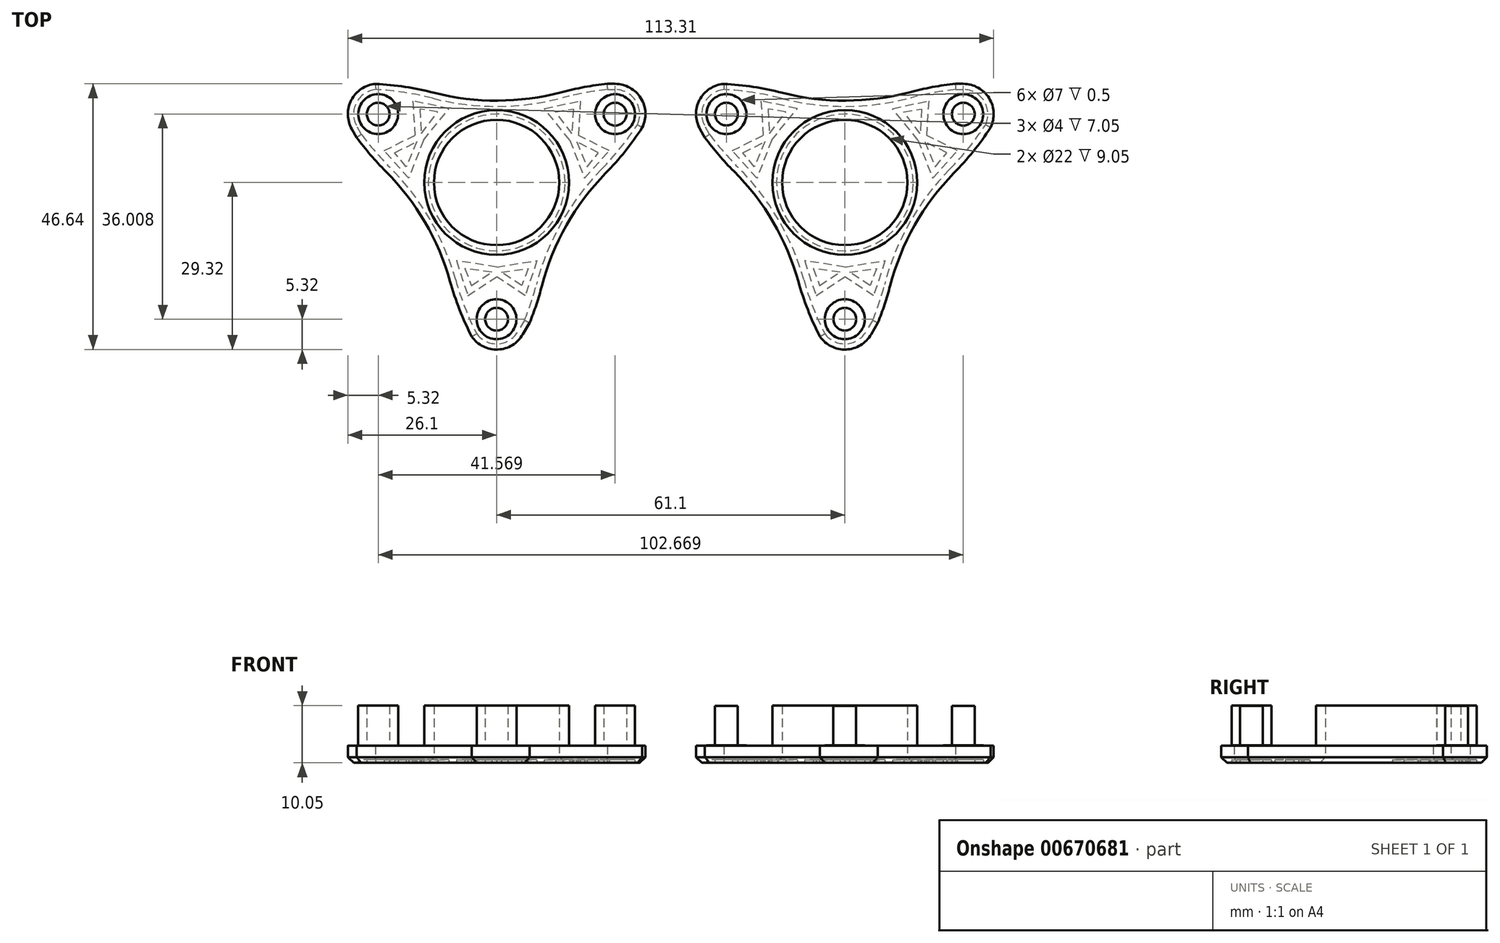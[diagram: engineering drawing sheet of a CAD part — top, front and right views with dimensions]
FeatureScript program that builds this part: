
annotation { "Feature Type Name" : "Feature", "Feature Type Description" : "" }
export const myFeature = defineFeature(function(context is Context, id is Id, definition is map)
    precondition{}
    {
        {
            var Q0;
            Q0=qCreatedBy(makeId("Top.planeOp"),FACE);
            var sketch = newSketch(context, id + "F0", { "sketchPlane" : qUnion([Q0])});
            skLineSegment(sketch, "E0.0", {"start": v(-30, 17.3) * mm, "end": v(30, 17.33) * mm});
            skLineSegment(sketch, "E0.1", {"start": v(30, 17.33) * mm, "end": v(0.02, -34.64) * mm});
            skLineSegment(sketch, "E0.2", {"start": v(0.02, -34.64) * mm, "end": v(-30, 17.3) * mm});
            skPoint(sketch, "E0.0.midPoint", {"position": v(0, 17.32) * mm});
            skLineSegment(sketch, "E1.0", {"start": v(0, 59) * mm, "end": v(50.95, -29.25) * mm, "construction": true});
            skLineSegment(sketch, "E1.1", {"start": v(50.95, -29.25) * mm, "end": v(-50.66, -29.25) * mm, "construction": true});
            skLineSegment(sketch, "E1.2", {"start": v(-50.66, -29.25) * mm, "end": v(0, 59) * mm, "construction": true});
            skCircle(sketch, "E2", {"center": v(-50.66, -29.25) * mm, "radius": 44.13 * mm});
            skCircle(sketch, "E3.1.0", {"center": v(50.66, -29.25) * mm, "radius": 44.13 * mm});
            skCircle(sketch, "E3.2.0", {"center": v(0, 58.5) * mm, "radius": 44.13 * mm});
            skPoint(sketch, "E3.center", {"position": v(0, 0) * mm});
            skPoint(sketch, "E4.0.midPoint", {"position": v(0, 14.36) * mm});
            skCircle(sketch, "E5", {"center": v(-20.78, 12) * mm, "radius": 3.5 * mm});
            skCircle(sketch, "E6.1.0", {"center": v(0, -24) * mm, "radius": 3.5 * mm});
            skCircle(sketch, "E6.2.0", {"center": v(20.79, 12) * mm, "radius": 3.5 * mm});
            skCircle(sketch, "E7", {"center": v(0, 0) * mm, "radius": 11 * mm});
            skCircle(sketch, "E8", {"center": v(0, 0) * mm, "radius": 12.7 * mm});
            skCircle(sketch, "E9", {"center": v(-20.78, 12) * mm, "radius": 2 * mm});
            skCircle(sketch, "E10.1.0", {"center": v(0, -24) * mm, "radius": 2 * mm});
            skCircle(sketch, "E10.2.0", {"center": v(20.79, 12) * mm, "radius": 2 * mm});
            skArc(sketch, "E11", {"start": v(25.22, 9.04) * mm, "mid": v(25.48, 14.5) * mm, "end": v(20.79, 17.32) * mm});
            skArc(sketch, "E12.1.0", {"start": v(-20.44, 17.32) * mm, "mid": v(-25.3, 14.81) * mm, "end": v(-25.4, 9.35) * mm});
            skArc(sketch, "E12.2.0", {"start": v(-4.78, -26.36) * mm, "mid": v(-0.18, -29.32) * mm, "end": v(4.6, -26.66) * mm});
            skLineSegment(sketch, "E13", {"start": v(20.79, 17.32) * mm, "end": v(19.44, 17.32) * mm});
            skLineSegment(sketch, "E14", {"start": v(-25.4, 9.35) * mm, "end": v(-24.56, 7.9) * mm});
            skLineSegment(sketch, "E15", {"start": v(-20.44, 17.32) * mm, "end": v(-19.08, 17.31) * mm});
            skLineSegment(sketch, "E16", {"start": v(25.22, 9.04) * mm, "end": v(24.03, 6.97) * mm});
            skLineSegment(sketch, "E17", {"start": v(4.6, -26.66) * mm, "end": v(5.8, -24.63) * mm});
            skLineSegment(sketch, "E18", {"start": v(-4.78, -26.36) * mm, "end": v(-5.84, -24.51) * mm});
            skLineSegment(sketch, "E19", {"start": v(-7.07, -13.73) * mm, "end": v(-5.04, -19.9) * mm});
            skLineSegment(sketch, "E20", {"start": v(-5.04, -19.9) * mm, "end": v(0, -16.56) * mm});
            skLineSegment(sketch, "E21", {"start": v(0, -14.83) * mm, "end": v(-7.07, -13.73) * mm});
            skLineSegment(sketch, "E22", {"start": v(-5.56, -15.13) * mm, "end": v(-4.42, -18.1) * mm});
            skLineSegment(sketch, "E23", {"start": v(-4.42, -18.1) * mm, "end": v(-0.83, -15.74) * mm});
            skLineSegment(sketch, "E24", {"start": v(-0.83, -15.74) * mm, "end": v(-5.56, -15.13) * mm});
            skLineSegment(sketch, "E25.MirrorCS", {"start": v(5.04, -19.9) * mm, "end": v(0, -16.56) * mm});
            skLineSegment(sketch, "E26.MirrorCS", {"start": v(7.07, -13.73) * mm, "end": v(5.04, -19.9) * mm});
            skLineSegment(sketch, "E27.MirrorCS", {"start": v(0.83, -15.74) * mm, "end": v(5.56, -15.13) * mm});
            skLineSegment(sketch, "E28.MirrorCS", {"start": v(5.56, -15.13) * mm, "end": v(4.42, -18.1) * mm});
            skLineSegment(sketch, "E29.MirrorCS", {"start": v(4.42, -18.1) * mm, "end": v(0.83, -15.74) * mm});
            skLineSegment(sketch, "E30.MirrorCS", {"start": v(0, -14.83) * mm, "end": v(7.07, -13.73) * mm});
            skLineSegment(sketch, "E31.1.0", {"start": v(15.42, 0.74) * mm, "end": v(19.75, 5.58) * mm});
            skLineSegment(sketch, "E31.1.1", {"start": v(12.85, 7.42) * mm, "end": v(15.42, 0.74) * mm});
            skLineSegment(sketch, "E31.1.2", {"start": v(14.04, 7.15) * mm, "end": v(15.89, 2.76) * mm});
            skLineSegment(sketch, "E31.1.3", {"start": v(17.88, 5.22) * mm, "end": v(14.04, 7.15) * mm});
            skLineSegment(sketch, "E31.1.4", {"start": v(15.89, 2.76) * mm, "end": v(17.88, 5.22) * mm});
            skLineSegment(sketch, "E31.1.5", {"start": v(19.75, 5.58) * mm, "end": v(14.34, 8.28) * mm});
            skLineSegment(sketch, "E31.1.6", {"start": v(14.7, 14.31) * mm, "end": v(14.34, 8.28) * mm});
            skLineSegment(sketch, "E31.1.7", {"start": v(13.46, 12.88) * mm, "end": v(13.22, 8.58) * mm});
            skLineSegment(sketch, "E31.1.8", {"start": v(13.22, 8.58) * mm, "end": v(10.33, 12.38) * mm});
            skLineSegment(sketch, "E31.1.9", {"start": v(10.33, 12.38) * mm, "end": v(13.46, 12.88) * mm});
            skLineSegment(sketch, "E31.1.10", {"start": v(12.85, 7.42) * mm, "end": v(8.35, 12.98) * mm});
            skLineSegment(sketch, "E31.1.11", {"start": v(8.35, 12.98) * mm, "end": v(14.7, 14.31) * mm});
            skLineSegment(sketch, "E31.2.0", {"start": v(-8.35, 12.98) * mm, "end": v(-14.7, 14.31) * mm});
            skLineSegment(sketch, "E31.2.1", {"start": v(-12.85, 7.42) * mm, "end": v(-8.35, 12.98) * mm});
            skLineSegment(sketch, "E31.2.2", {"start": v(-13.22, 8.58) * mm, "end": v(-10.33, 12.38) * mm});
            skLineSegment(sketch, "E31.2.3", {"start": v(-13.46, 12.88) * mm, "end": v(-13.22, 8.58) * mm});
            skLineSegment(sketch, "E31.2.4", {"start": v(-10.33, 12.38) * mm, "end": v(-13.46, 12.88) * mm});
            skLineSegment(sketch, "E31.2.5", {"start": v(-14.7, 14.31) * mm, "end": v(-14.34, 8.28) * mm});
            skLineSegment(sketch, "E31.2.6", {"start": v(-19.75, 5.58) * mm, "end": v(-14.34, 8.28) * mm});
            skLineSegment(sketch, "E31.2.7", {"start": v(-17.88, 5.22) * mm, "end": v(-14.04, 7.15) * mm});
            skLineSegment(sketch, "E31.2.8", {"start": v(-14.04, 7.15) * mm, "end": v(-15.89, 2.76) * mm});
            skLineSegment(sketch, "E31.2.9", {"start": v(-15.89, 2.76) * mm, "end": v(-17.88, 5.22) * mm});
            skLineSegment(sketch, "E31.2.10", {"start": v(-12.85, 7.42) * mm, "end": v(-15.42, 0.74) * mm});
            skLineSegment(sketch, "E31.2.11", {"start": v(-15.42, 0.74) * mm, "end": v(-19.75, 5.58) * mm});
            skSolve(sketch);
        }
        {
            var Q0;
            Q0=makeQuery(id+"F0.imprint","IMPRINT",FACE,{"disambiguationData":[TD([[makeQuery(id+"F0.imprint","IMPRINT",EDGE,{"derivedFrom":sQuery(id+"F0.wireOp",EDGE,"E5")}),-1.0]])]});
            var Q1;
            Q1=makeQuery(id+"F0.imprint","IMPRINT",FACE,{"disambiguationData":[TD([[makeQuery(id+"F0.imprint","IMPRINT",EDGE,{"derivedFrom":sQuery(id+"F0.wireOp",EDGE,"E9")}),1.0]])]});
            var Q2;
            Q2=makeQuery(id+"F0.imprint","IMPRINT",FACE,{"disambiguationData":[TD([[makeQuery(id+"F0.imprint","IMPRINT",EDGE,{"derivedFrom":sQuery(id+"F0.wireOp",EDGE,"E10.2.0")}),1.0]])]});
            var Q3;
            Q3=makeQuery(id+"F0.imprint","IMPRINT",FACE,{"disambiguationData":[TD([[makeQuery(id+"F0.imprint","IMPRINT",EDGE,{"derivedFrom":sQuery(id+"F0.wireOp",EDGE,"E10.1.0")}),1.0]])]});
            var Q4;
            Q4=makeQuery(id+"F0.imprint","IMPRINT",FACE,{"disambiguationData":[TD([[makeQuery(id+"F0.imprint","IMPRINT",EDGE,{"derivedFrom":sQuery(id+"F0.wireOp",EDGE,"E19")}),1.0]])]});
            var Q5;
            Q5=makeQuery(id+"F0.imprint","IMPRINT",FACE,{"disambiguationData":[TD([[makeQuery(id+"F0.imprint","IMPRINT",EDGE,{"derivedFrom":sQuery(id+"F0.wireOp",EDGE,"E27.MirrorCS")}),-1.0]])]});
            var Q6;
            Q6=makeQuery(id+"F0.imprint","IMPRINT",FACE,{"disambiguationData":[TD([[makeQuery(id+"F0.imprint","IMPRINT",EDGE,{"derivedFrom":sQuery(id+"F0.wireOp",EDGE,"E22")}),1.0]])]});
            var Q7;
            Q7=makeQuery(id+"F0.imprint","IMPRINT",FACE,{"disambiguationData":[TD([[makeQuery(id+"F0.imprint","IMPRINT",EDGE,{"derivedFrom":sQuery(id+"F0.wireOp",EDGE,"E31.1.0")}),1.0]])]});
            var Q8;
            Q8=makeQuery(id+"F0.imprint","IMPRINT",FACE,{"disambiguationData":[TD([[makeQuery(id+"F0.imprint","IMPRINT",EDGE,{"derivedFrom":sQuery(id+"F0.wireOp",EDGE,"E31.1.2")}),1.0]])]});
            var Q9;
            Q9=makeQuery(id+"F0.imprint","IMPRINT",FACE,{"disambiguationData":[TD([[makeQuery(id+"F0.imprint","IMPRINT",EDGE,{"derivedFrom":sQuery(id+"F0.wireOp",EDGE,"E31.1.7")}),-1.0]])]});
            var Q10;
            Q10=makeQuery(id+"F0.imprint","IMPRINT",FACE,{"disambiguationData":[TD([[makeQuery(id+"F0.imprint","IMPRINT",EDGE,{"derivedFrom":sQuery(id+"F0.wireOp",EDGE,"E31.2.0")}),1.0]])]});
            var Q11;
            Q11=makeQuery(id+"F0.imprint","IMPRINT",FACE,{"disambiguationData":[TD([[makeQuery(id+"F0.imprint","IMPRINT",EDGE,{"derivedFrom":sQuery(id+"F0.wireOp",EDGE,"E31.2.2")}),1.0]])]});
            var Q12;
            Q12=makeQuery(id+"F0.imprint","IMPRINT",FACE,{"disambiguationData":[TD([[makeQuery(id+"F0.imprint","IMPRINT",EDGE,{"derivedFrom":sQuery(id+"F0.wireOp",EDGE,"E31.2.7")}),-1.0]])]});
            extrude(context, id + "F1", {"entities" : qUnion([Q0, Q1, Q2, Q3, Q4, Q5, Q6, Q7, Q8, Q9, Q10, Q11, Q12]), "depth" : 3 * mm, "offsetDistance" : 25 * mm});
        }
        {
            var Q0;
            Q0=makeQuery(id+"F0.imprint","IMPRINT",FACE,{"disambiguationData":[TD([[makeQuery(id+"F0.imprint","IMPRINT",EDGE,{"derivedFrom":sQuery(id+"F0.wireOp",EDGE,"E5")}),1.0]])]});
            var Q1;
            Q1=makeQuery(id+"F0.imprint","IMPRINT",FACE,{"disambiguationData":[TD([[makeQuery(id+"F0.imprint","IMPRINT",EDGE,{"derivedFrom":sQuery(id+"F0.wireOp",EDGE,"E6.1.0")}),1.0]])]});
            var Q2;
            Q2=makeQuery(id+"F0.imprint","IMPRINT",FACE,{"disambiguationData":[TD([[makeQuery(id+"F0.imprint","IMPRINT",EDGE,{"derivedFrom":sQuery(id+"F0.wireOp",EDGE,"E6.2.0")}),1.0]])]});
            var Q3;
            Q3=makeQuery(id+"F0.imprint","IMPRINT",FACE,{"disambiguationData":[TD([[makeQuery(id+"F0.imprint","IMPRINT",EDGE,{"derivedFrom":sQuery(id+"F0.wireOp",EDGE,"E7")}),-1.0]])]});
            extrude(context, id + "F2", {"entities" : qUnion([Q0, Q1, Q2, Q3]), "operationType" : NewBodyOperationType.ADD, "depth" : 10.05 * mm, "offsetDistance" : 25 * mm});
        }
        {
            var Q0;
            {var subQ0=sQuery(id+"F0.wireOp",EDGE,"E3.1.0");var subQ1=sQuery(id+"F0.wireOp",EDGE,"E0.1");Q0=makeQuery(id+"F1.opExtrude","SWEPT_EDGE",EDGE,{"disambiguationData":[OSD([subQ1,subQ0]),TDD([makeQuery(id+"F0.imprint","INTERSECT",VERTEX,{"disambiguationData":[OD(0.0)],"derivedFrom":[subQ1,subQ0]})])]});}
            var Q1;
            {var subQ0=sQuery(id+"F0.wireOp",EDGE,"E3.2.0");var subQ1=sQuery(id+"F0.wireOp",EDGE,"E0.0");Q1=makeQuery(id+"F1.opExtrude","SWEPT_EDGE",EDGE,{"disambiguationData":[OSD([subQ1,subQ0]),TDD([makeQuery(id+"F0.imprint","INTERSECT",VERTEX,{"disambiguationData":[OD(1.0)],"derivedFrom":[subQ1,subQ0]})])]});}
            var Q2;
            {var subQ0=sQuery(id+"F0.wireOp",EDGE,"E3.2.0");var subQ1=sQuery(id+"F0.wireOp",EDGE,"E0.0");Q2=makeQuery(id+"F1.opExtrude","SWEPT_EDGE",EDGE,{"disambiguationData":[OSD([subQ1,subQ0]),TDD([makeQuery(id+"F0.imprint","INTERSECT",VERTEX,{"disambiguationData":[OD(0.0)],"derivedFrom":[subQ1,subQ0]})])]});}
            var Q3;
            {var subQ0=sQuery(id+"F0.wireOp",EDGE,"E2");var subQ1=sQuery(id+"F0.wireOp",EDGE,"E0.2");Q3=makeQuery(id+"F1.opExtrude","SWEPT_EDGE",EDGE,{"disambiguationData":[OSD([subQ1,subQ0]),TDD([makeQuery(id+"F0.imprint","INTERSECT",VERTEX,{"disambiguationData":[OD(1.0)],"derivedFrom":[subQ1,subQ0]})])]});}
            var Q4;
            {var subQ0=sQuery(id+"F0.wireOp",EDGE,"E2");var subQ1=sQuery(id+"F0.wireOp",EDGE,"E0.2");Q4=makeQuery(id+"F1.opExtrude","SWEPT_EDGE",EDGE,{"disambiguationData":[OSD([subQ1,subQ0]),TDD([makeQuery(id+"F0.imprint","INTERSECT",VERTEX,{"disambiguationData":[OD(0.0)],"derivedFrom":[subQ1,subQ0]})])]});}
            var Q5;
            {var subQ0=sQuery(id+"F0.wireOp",EDGE,"E3.1.0");var subQ1=sQuery(id+"F0.wireOp",EDGE,"E0.1");Q5=makeQuery(id+"F1.opExtrude","SWEPT_EDGE",EDGE,{"disambiguationData":[OSD([subQ1,subQ0]),TDD([makeQuery(id+"F0.imprint","INTERSECT",VERTEX,{"disambiguationData":[OD(1.0)],"derivedFrom":[subQ1,subQ0]})])]});}
            fillet(context, id + "F3", {"entities" : qUnion([Q0, Q1, Q2, Q3, Q4, Q5]), "radius" : 52.19 * mm, "tangentPropagation" : true, "allowEdgeOverflow" : false});
        }
        {
            var Q0;
            {var subQ0=sQuery(id+"F0.wireOp",EDGE,"E8");var subQ1=sQuery(id+"F0.wireOp",EDGE,"E10.2.0");var subQ2=sQuery(id+"F0.wireOp",EDGE,"E6.2.0");var subQ3=sQuery(id+"F0.wireOp",EDGE,"E10.1.0");var subQ4=sQuery(id+"F0.wireOp",EDGE,"E6.1.0");var subQ5=sQuery(id+"F0.wireOp",EDGE,"E9");var subQ6=sQuery(id+"F0.wireOp",EDGE,"E5");Q0=makeQuery(id+"F2.boolean.opBoolean","MERGE",FACE,{"derivedFrom":[makeQuery(id+"F1.opExtrude","CAP_FACE",FACE,{"disambiguationData":[OSD([sQuery(id+"F0.wireOp",EDGE,"E0.0"),sQuery(id+"F0.wireOp",EDGE,"E0.1"),sQuery(id+"F0.wireOp",EDGE,"E0.2"),sQuery(id+"F0.wireOp",EDGE,"E2"),sQuery(id+"F0.wireOp",EDGE,"E3.1.0"),sQuery(id+"F0.wireOp",EDGE,"E3.2.0"),subQ6,subQ4,subQ2,subQ0,sQuery(id+"F0.wireOp",EDGE,"1SJySKtc-A8GW-sxNI-XXrC-uOoADmk9XYJx"),sQuery(id+"F0.wireOp",EDGE,"85b40759-12c6-4cf2-8159-2576a97e2fa2.1.0"),sQuery(id+"F0.wireOp",EDGE,"85b40759-12c6-4cf2-8159-2576a97e2fa2.2.0"),sQuery(id+"F0.wireOp",EDGE,"dcBHJXyL-KOau-6C6y-PPaA-2r918rPn5gXJ"),sQuery(id+"F0.wireOp",EDGE,"AZoCeLLD-ZZL2-adv5-qf0w-prbMICUiqzPw"),sQuery(id+"F0.wireOp",EDGE,"4dO1bbNr-65Ks-fPpC-CJ1R-cWI9Ptmbnuol")])],"isStart":true}),makeQuery(id+"F1.opExtrude","CAP_FACE",FACE,{"disambiguationData":[OSD([subQ5])],"isStart":true}),makeQuery(id+"F1.opExtrude","CAP_FACE",FACE,{"disambiguationData":[OSD([subQ3])],"isStart":true}),makeQuery(id+"F1.opExtrude","CAP_FACE",FACE,{"disambiguationData":[OSD([subQ1])],"isStart":true}),makeQuery(id+"F2.opExtrude","CAP_FACE",FACE,{"disambiguationData":[OSD([subQ6,subQ5])],"isStart":true}),makeQuery(id+"F2.opExtrude","CAP_FACE",FACE,{"disambiguationData":[OSD([subQ4,subQ3])],"isStart":true}),makeQuery(id+"F2.opExtrude","CAP_FACE",FACE,{"disambiguationData":[OSD([subQ2,subQ1])],"isStart":true}),makeQuery(id+"F2.opExtrude","CAP_FACE",FACE,{"disambiguationData":[OSD([sQuery(id+"F0.wireOp",EDGE,"E7"),subQ0])],"isStart":true})]});}
            chamfer(context, id + "F4", {"entities" : qUnion([Q0]), "width" : 1 * mm, "tangentPropagation" : true});
        }
        {
            var Q0;
            Q0=makeQuery(id+"F1.opExtrude","SWEPT_BODY",BODY,{"disambiguationData":[OSD([sQuery(id+"F0.wireOp",EDGE,"E0.0"),sQuery(id+"F0.wireOp",EDGE,"E0.1"),sQuery(id+"F0.wireOp",EDGE,"E0.2"),sQuery(id+"F0.wireOp",EDGE,"E2"),sQuery(id+"F0.wireOp",EDGE,"E3.1.0"),sQuery(id+"F0.wireOp",EDGE,"E3.2.0"),sQuery(id+"F0.wireOp",EDGE,"E5"),sQuery(id+"F0.wireOp",EDGE,"E6.1.0"),sQuery(id+"F0.wireOp",EDGE,"E6.2.0"),sQuery(id+"F0.wireOp",EDGE,"E8"),sQuery(id+"F0.wireOp",EDGE,"E11"),sQuery(id+"F0.wireOp",EDGE,"E12.1.0"),sQuery(id+"F0.wireOp",EDGE,"E12.2.0"),sQuery(id+"F0.wireOp",EDGE,"E13"),sQuery(id+"F0.wireOp",EDGE,"E14"),sQuery(id+"F0.wireOp",EDGE,"E16"),sQuery(id+"F0.wireOp",EDGE,"E17")])]});
            transform(context, id + "F5", {"entities" : qUnion([Q0]), "transformType" : TransformType.TRANSLATION_3D, "dx" : 61 * mm, "dy" : 0 * mm, "dz" : 0 * mm, "makeCopy" : true});
        }
        {
            var Q0;
            Q0=makeQuery(id+"F0.imprint","IMPRINT",FACE,{"disambiguationData":[TD([[makeQuery(id+"F0.imprint","IMPRINT",EDGE,{"derivedFrom":sQuery(id+"F0.wireOp",EDGE,"E31.2.0")}),1.0]])]});
            var Q1;
            Q1=makeQuery(id+"F0.imprint","IMPRINT",FACE,{"disambiguationData":[TD([[makeQuery(id+"F0.imprint","IMPRINT",EDGE,{"derivedFrom":sQuery(id+"F0.wireOp",EDGE,"E6.2.0")}),1.0]])]});
            var Q2;
            Q2=makeQuery(id+"F0.imprint","IMPRINT",FACE,{"disambiguationData":[TD([[makeQuery(id+"F0.imprint","IMPRINT",EDGE,{"derivedFrom":sQuery(id+"F0.wireOp",EDGE,"E31.1.0")}),1.0]])]});
            var Q3;
            Q3=makeQuery(id+"F0.imprint","IMPRINT",FACE,{"disambiguationData":[TD([[makeQuery(id+"F0.imprint","IMPRINT",EDGE,{"derivedFrom":sQuery(id+"F0.wireOp",EDGE,"E19")}),1.0]])]});
            var Q4;
            Q4=makeQuery(id+"F0.imprint","IMPRINT",FACE,{"disambiguationData":[TD([[makeQuery(id+"F0.imprint","IMPRINT",EDGE,{"derivedFrom":sQuery(id+"F0.wireOp",EDGE,"E6.1.0")}),1.0]])]});
            var Q5;
            Q5=makeQuery(id+"F0.imprint","IMPRINT",FACE,{"disambiguationData":[TD([[makeQuery(id+"F0.imprint","IMPRINT",EDGE,{"derivedFrom":sQuery(id+"F0.wireOp",EDGE,"E5")}),1.0]])]});
            extrude(context, id + "F6", {"entities" : qUnion([Q0, Q1, Q2, Q3, Q4, Q5]), "operationType" : NewBodyOperationType.REMOVE, "depth" : 0.5 * mm, "offsetDistance" : 25 * mm});
        }
        {
            var Q0;
            Q0=makeQuery(id+"F5.opPattern","COPY",BODY,{"derivedFrom":makeQuery(id+"F1.opExtrude","SWEPT_BODY",BODY,{"disambiguationData":[OSD([sQuery(id+"F0.wireOp",EDGE,"E0.0"),sQuery(id+"F0.wireOp",EDGE,"E0.1"),sQuery(id+"F0.wireOp",EDGE,"E0.2"),sQuery(id+"F0.wireOp",EDGE,"E2"),sQuery(id+"F0.wireOp",EDGE,"E3.1.0"),sQuery(id+"F0.wireOp",EDGE,"E3.2.0"),sQuery(id+"F0.wireOp",EDGE,"E5"),sQuery(id+"F0.wireOp",EDGE,"E6.1.0"),sQuery(id+"F0.wireOp",EDGE,"E6.2.0"),sQuery(id+"F0.wireOp",EDGE,"E8"),sQuery(id+"F0.wireOp",EDGE,"E11"),sQuery(id+"F0.wireOp",EDGE,"E12.1.0"),sQuery(id+"F0.wireOp",EDGE,"E12.2.0"),sQuery(id+"F0.wireOp",EDGE,"E13"),sQuery(id+"F0.wireOp",EDGE,"E14"),sQuery(id+"F0.wireOp",EDGE,"E16"),sQuery(id+"F0.wireOp",EDGE,"E17")])]}),"instanceName":"1"});
            deleteBodies(context, id + "F7", {"entities" : qUnion([Q0])});
        }
        {
            var Q0;
            Q0=makeQuery(id+"F1.opExtrude","SWEPT_BODY",BODY,{"disambiguationData":[OSD([sQuery(id+"F0.wireOp",EDGE,"E0.0"),sQuery(id+"F0.wireOp",EDGE,"E0.1"),sQuery(id+"F0.wireOp",EDGE,"E0.2"),sQuery(id+"F0.wireOp",EDGE,"E2"),sQuery(id+"F0.wireOp",EDGE,"E3.1.0"),sQuery(id+"F0.wireOp",EDGE,"E3.2.0"),sQuery(id+"F0.wireOp",EDGE,"E5"),sQuery(id+"F0.wireOp",EDGE,"E6.1.0"),sQuery(id+"F0.wireOp",EDGE,"E6.2.0"),sQuery(id+"F0.wireOp",EDGE,"E8"),sQuery(id+"F0.wireOp",EDGE,"E11"),sQuery(id+"F0.wireOp",EDGE,"E12.1.0"),sQuery(id+"F0.wireOp",EDGE,"E12.2.0"),sQuery(id+"F0.wireOp",EDGE,"E13"),sQuery(id+"F0.wireOp",EDGE,"E14"),sQuery(id+"F0.wireOp",EDGE,"E16"),sQuery(id+"F0.wireOp",EDGE,"E17")])]});
            transform(context, id + "F8", {"entities" : qUnion([Q0]), "transformType" : TransformType.TRANSLATION_3D, "dx" : 61.1 * mm, "dy" : 0 * mm, "dz" : 0 * mm, "makeCopy" : true});
        }
        {
            var Q0;
            Q0=makeQuery(id+"F8.opPattern","COPY",FACE,{"derivedFrom":makeQuery(id+"F2.opExtrude","CAP_FACE",FACE,{"disambiguationData":[OSD([sQuery(id+"F0.wireOp",EDGE,"E5"),sQuery(id+"F0.wireOp",EDGE,"E9")])],"isStart":false}),"instanceName":"1"});
            var Q1;
            Q1=makeQuery(id+"F8.opPattern","COPY",FACE,{"derivedFrom":makeQuery(id+"F2.opExtrude","CAP_FACE",FACE,{"disambiguationData":[OSD([sQuery(id+"F0.wireOp",EDGE,"E6.2.0"),sQuery(id+"F0.wireOp",EDGE,"E10.2.0")])],"isStart":false}),"instanceName":"1"});
            var Q2;
            Q2=makeQuery(id+"F8.opPattern","COPY",FACE,{"derivedFrom":makeQuery(id+"F2.opExtrude","CAP_FACE",FACE,{"disambiguationData":[OSD([sQuery(id+"F0.wireOp",EDGE,"E6.1.0"),sQuery(id+"F0.wireOp",EDGE,"E10.1.0")])],"isStart":false}),"instanceName":"1"});
            extrude(context, id + "F9", {"entities" : qUnion([Q0, Q1, Q2]), "operationType" : NewBodyOperationType.REMOVE, "oppositeDirection" : true, "depth" : 7 * mm, "offsetDistance" : 25 * mm});
        }
        {
            var Q0;
            Q0=makeQuery(id+"F8.opPattern","COPY",FACE,{"derivedFrom":makeQuery(id+"F1.opExtrude","CAP_FACE",FACE,{"disambiguationData":[OSD([sQuery(id+"F0.wireOp",EDGE,"E9")])],"isStart":false}),"instanceName":"1"});
            var Q1;
            Q1=makeQuery(id+"F8.opPattern","COPY",FACE,{"derivedFrom":makeQuery(id+"F1.opExtrude","CAP_FACE",FACE,{"disambiguationData":[OSD([sQuery(id+"F0.wireOp",EDGE,"E10.2.0")])],"isStart":false}),"instanceName":"1"});
            var Q2;
            Q2=makeQuery(id+"F8.opPattern","COPY",FACE,{"derivedFrom":makeQuery(id+"F1.opExtrude","CAP_FACE",FACE,{"disambiguationData":[OSD([sQuery(id+"F0.wireOp",EDGE,"E10.1.0")])],"isStart":false}),"instanceName":"1"});
            extrude(context, id + "F10", {"entities" : qUnion([Q0, Q1, Q2]), "operationType" : NewBodyOperationType.ADD, "depth" : 7 * mm, "offsetDistance" : 25 * mm});
        }
    });
